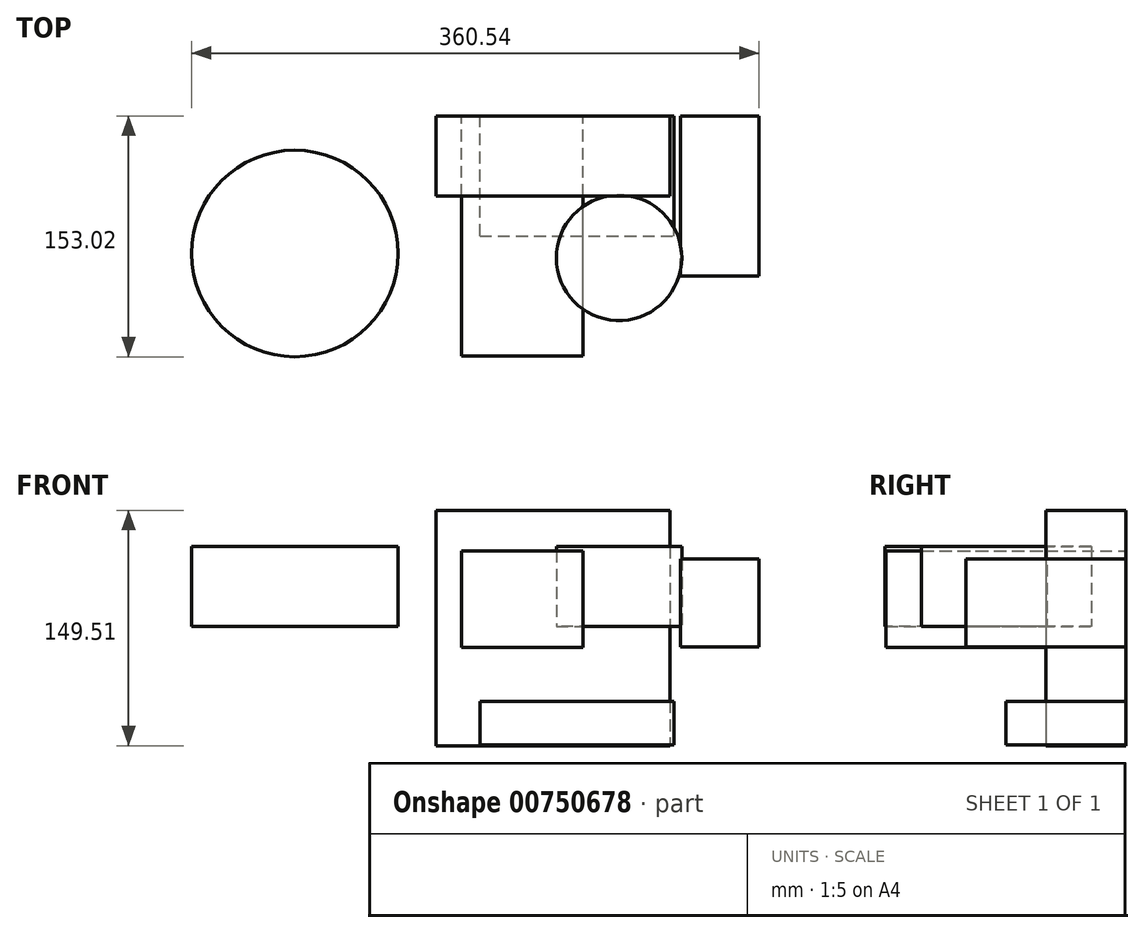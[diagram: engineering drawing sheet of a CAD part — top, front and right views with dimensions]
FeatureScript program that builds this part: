
annotation { "Feature Type Name" : "Feature", "Feature Type Description" : "" }
export const myFeature = defineFeature(function(context is Context, id is Id, definition is map)
    precondition{}
    {
        {
            var Q0;
            Q0=qCreatedBy(makeId("Front.planeOp"),FACE);
            var sketch = newSketch(context, id + "F0", { "sketchPlane" : qUnion([Q0])});
            skLineSegment(sketch, "E0.bottom", {"start": v(-55.79, 48.16) * mm, "end": v(21.53, 48.16) * mm});
            skLineSegment(sketch, "E0.top", {"start": v(-55.79, -13.28) * mm, "end": v(21.53, -13.28) * mm});
            skLineSegment(sketch, "E0.left", {"start": v(-55.79, 48.16) * mm, "end": v(-55.79, -13.28) * mm});
            skLineSegment(sketch, "E0.right", {"start": v(21.53, 48.16) * mm, "end": v(21.53, -13.28) * mm});
            skSolve(sketch);
        }
        {
            var Q0;
            Q0=makeQuery(id+"F0.imprint","IMPRINT",FACE,{"disambiguationData":[TD([[makeQuery(id+"F0.imprint","IMPRINT",EDGE,{"derivedFrom":sQuery(id+"F0.wireOp",EDGE,"E0.bottom")}),-1.0]])]});
            extrude(context, id + "F1", {"entities" : qUnion([Q0]), "depth" : 50.8 * mm, "offsetDistance" : 25.4 * mm});
        }
        {
            var Q0;
            Q0=qCreatedBy(makeId("Front.planeOp"),FACE);
            var sketch = newSketch(context, id + "F2", { "sketchPlane" : qUnion([Q0])});
            skLineSegment(sketch, "E1.bottom", {"start": v(83.41, 43.03) * mm, "end": v(133.33, 43.03) * mm});
            skLineSegment(sketch, "E1.top", {"start": v(83.41, -12.78) * mm, "end": v(133.33, -12.78) * mm});
            skLineSegment(sketch, "E1.left", {"start": v(83.41, 43.03) * mm, "end": v(83.41, -12.78) * mm});
            skLineSegment(sketch, "E1.right", {"start": v(133.33, 43.03) * mm, "end": v(133.33, -12.78) * mm});
            skSolve(sketch);
        }
        {
            var Q0;
            Q0=makeQuery(id+"F2.imprint","IMPRINT",FACE,{"disambiguationData":[TD([[makeQuery(id+"F2.imprint","IMPRINT",EDGE,{"derivedFrom":sQuery(id+"F2.wireOp",EDGE,"E1.bottom")}),-1.0]])]});
            extrude(context, id + "F3", {"entities" : qUnion([Q0]), "depth" : 101.6 * mm, "offsetDistance" : 25.4 * mm});
        }
        {
            var Q0;
            Q0=qCreatedBy(makeId("Front.planeOp"),FACE);
            var sketch = newSketch(context, id + "F4", { "sketchPlane" : qUnion([Q0])});
            skLineSegment(sketch, "E2.bottom", {"start": v(-44.08, -47.45) * mm, "end": v(79.14, -47.45) * mm});
            skLineSegment(sketch, "E2.top", {"start": v(-44.08, -75.22) * mm, "end": v(79.14, -75.22) * mm});
            skLineSegment(sketch, "E2.left", {"start": v(-44.08, -47.45) * mm, "end": v(-44.08, -75.22) * mm});
            skLineSegment(sketch, "E2.right", {"start": v(79.14, -47.45) * mm, "end": v(79.14, -75.22) * mm});
            skSolve(sketch);
        }
        {
            var Q0;
            Q0 = qSketchRegion(id + "F4", true);
            extrude(context, id + "F5", {"entities" : qUnion([Q0]), "depth" : 76.2 * mm, "offsetDistance" : 25.4 * mm});
        }
        {
            var Q0;
            Q0=qCreatedBy(makeId("Front.planeOp"),FACE);
            var sketch = newSketch(context, id + "F6", { "sketchPlane" : qUnion([Q0])});
            skLineSegment(sketch, "E3.bottom", {"start": v(-71.82, 73.92) * mm, "end": v(76.62, 73.92) * mm});
            skLineSegment(sketch, "E3.top", {"start": v(-71.82, -75.59) * mm, "end": v(76.62, -75.59) * mm});
            skLineSegment(sketch, "E3.left", {"start": v(-71.82, 73.92) * mm, "end": v(-71.82, -75.59) * mm});
            skLineSegment(sketch, "E3.right", {"start": v(76.62, 73.92) * mm, "end": v(76.62, -75.59) * mm});
            skSolve(sketch);
        }
        {
            var Q0;
            Q0=makeQuery(id+"F6.imprint","IMPRINT",FACE,{"disambiguationData":[TD([[makeQuery(id+"F6.imprint","IMPRINT",EDGE,{"derivedFrom":sQuery(id+"F6.wireOp",EDGE,"E3.bottom")}),-1.0]])]});
            extrude(context, id + "F7", {"entities" : qUnion([Q0]), "depth" : 50.8 * mm, "offsetDistance" : 25.4 * mm});
        }
        {
            var Q0;
            Q0=makeQuery(id+"F1.opExtrude","CAP_FACE",FACE,{"disambiguationData":[OSD([sQuery(id+"F0.wireOp",EDGE,"E0.bottom"),sQuery(id+"F0.wireOp",EDGE,"E0.top"),sQuery(id+"F0.wireOp",EDGE,"E0.left"),sQuery(id+"F0.wireOp",EDGE,"E0.right")])],"isStart":false});
            extrude(context, id + "F8", {"entities" : qUnion([Q0]), "depth" : 101.6 * mm, "offsetDistance" : 25.4 * mm});
        }
        {
            var Q0;
            Q0=qCreatedBy(makeId("Top.planeOp"),FACE);
            var sketch = newSketch(context, id + "F9", { "sketchPlane" : qUnion([Q0])});
            skCircle(sketch, "E4", {"center": v(-161.62, -87.44) * mm, "radius": 65.58 * mm});
            skSolve(sketch);
        }
        {
            var Q0;
            Q0=makeQuery(id+"F9.imprint","IMPRINT",FACE,{"disambiguationData":[TD([[makeQuery(id+"F9.imprint","IMPRINT",EDGE,{"derivedFrom":sQuery(id+"F9.wireOp",EDGE,"E4")}),1.0]])]});
            extrude(context, id + "F10", {"entities" : qUnion([Q0]), "depth" : 50.8 * mm, "offsetDistance" : 25.4 * mm});
        }
        {
            var Q0;
            Q0=makeQuery(id+"F0.imprint","IMPRINT",FACE,{"disambiguationData":[TD([[makeQuery(id+"F0.imprint","IMPRINT",EDGE,{"derivedFrom":sQuery(id+"F0.wireOp",EDGE,"E0.bottom")}),-1.0]])]});
            extrude(context, id + "F11", {"entities" : qUnion([Q0]), "depth" : 50.8 * mm, "offsetDistance" : 25.4 * mm});
        }
        {
            var Q0;
            Q0=qCreatedBy(makeId("Right.planeOp"),FACE);
            var sketch = newSketch(context, id + "F12", { "sketchPlane" : qUnion([Q0])});
            skArc(sketch, "E5", {"start": v(318.07, -85.5) * mm, "mid": v(301.1, -74.03) * mm, "end": v(283.3, -63.92) * mm});
            skArc(sketch, "E6", {"start": v(340.7, -195.3) * mm, "mid": v(326.14, -185.77) * mm, "end": v(310.8, -177.55) * mm});
            skArc(sketch, "E7", {"start": v(-45.57, -18.03) * mm, "mid": v(-131.58, 126.96) * mm, "end": v(-160, -39.2) * mm});
            skSolve(sketch);
        }
        {
            var Q0;
            Q0=sQuery(id+"F12.wireOp",EDGE,"E7");
            extrude(context, id + "F13", {"bodyType" : ToolBodyType.SURFACE, "surfaceEntities" : qUnion([Q0]), "depth" : 127 * mm, "offsetDistance" : 25.4 * mm});
        }
        {
            var Q0;
            Q0=qCreatedBy(makeId("Top.planeOp"),FACE);
            var sketch = newSketch(context, id + "F14", { "sketchPlane" : qUnion([Q0])});
            skCircle(sketch, "E8", {"center": v(44.38, -90.16) * mm, "radius": 39.82 * mm});
            skSolve(sketch);
        }
        {
            var Q0;
            Q0=makeQuery(id+"F14.imprint","IMPRINT",FACE,{"disambiguationData":[TD([[makeQuery(id+"F14.imprint","IMPRINT",EDGE,{"derivedFrom":sQuery(id+"F14.wireOp",EDGE,"E8")}),1.0]])]});
            extrude(context, id + "F15", {"entities" : qUnion([Q0]), "depth" : 50.8 * mm, "offsetDistance" : 25.4 * mm});
        }
    });
